# Revit family: Furniture-Workstation-Midmark-Care_Exchange-6231-Mobile
name_source: partatom
category: Furniture
revit_build: Autodesk Revit 2016 (Build: 20170117_1200(x64)
units: mm (PartAtom-declared; Revit-internal decimal feet)

## family parameters
Always vertical = Yes
Cut with Voids When Loaded = No
OmniClass Number = 23.40.70.11.14.11
OmniClass Title = Medical Equipment
Room Calculation Point = No
Shared = No
Work Plane-Based = No

## types (1)
- 6231
    Counter Material = Paint-Midmark-Mist
    Description = Mobile Procedure Workstation
    Device Holder = Yes
    Equipment Pole = Yes
    Manufacturer = Midmark
    Model = 6231
    Product Documentation Link = http://www.midmark.com
    Product Name = MIDMARK 6231 - CARE EXCHANGE®
    Product Page URL = http://www.midmark.com
    Rear Basket = Yes
    Type Comments = The 6231 procedure workstation is designed to support many device workflows.
    URL = http://www.midmark.com

## geometry (parser evidence)
native form markers: Blend x2, Sweep x35
no freeform markers — native parametric forms only
